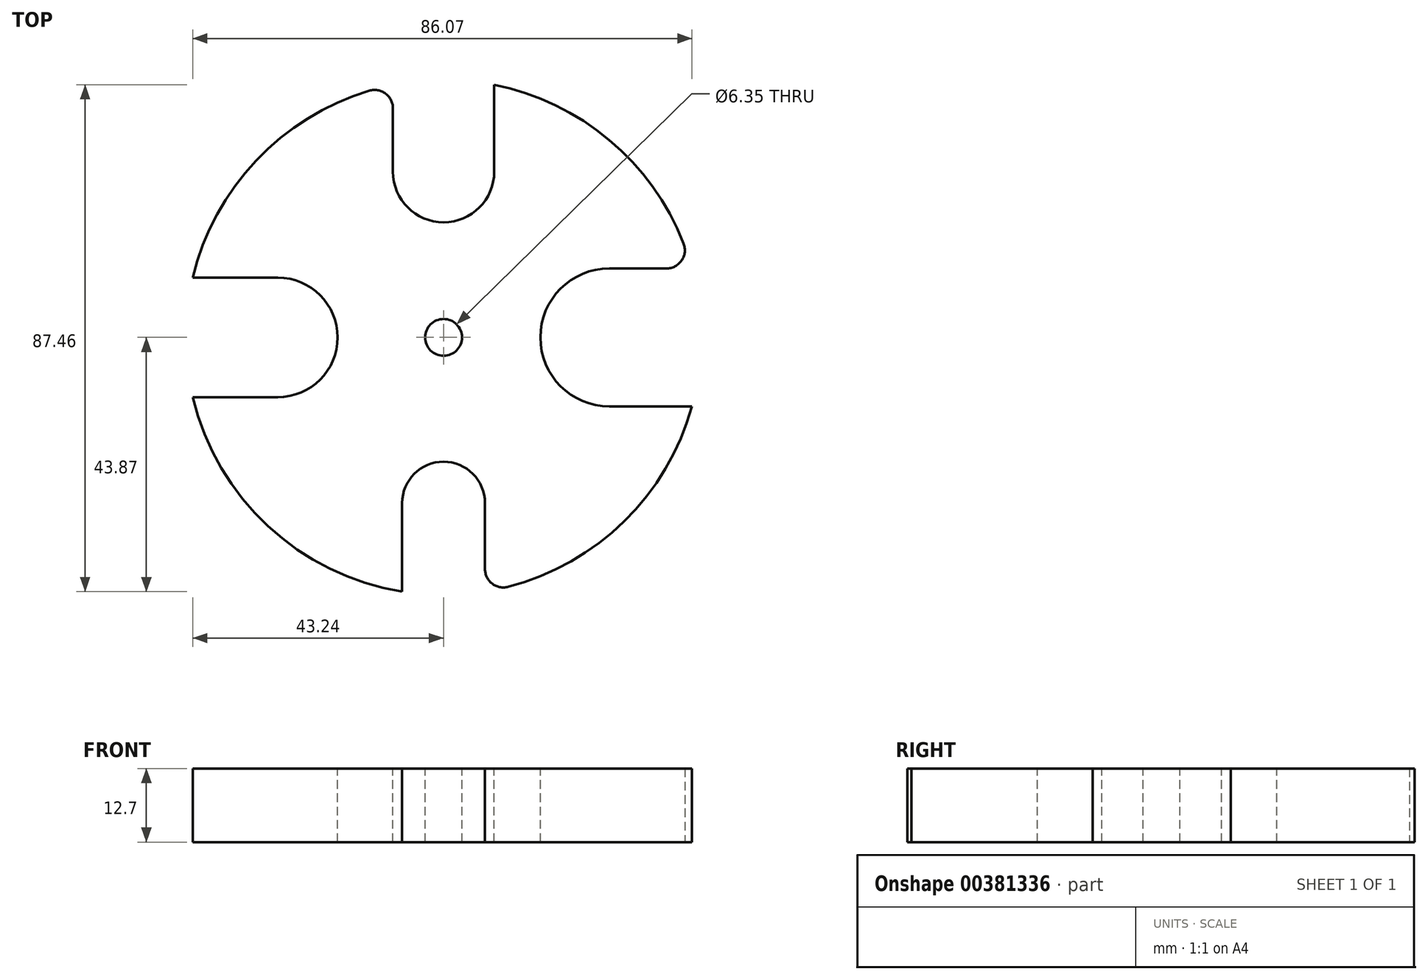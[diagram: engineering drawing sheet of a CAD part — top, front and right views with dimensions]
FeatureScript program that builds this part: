
annotation { "Feature Type Name" : "Feature", "Feature Type Description" : "" }
export const myFeature = defineFeature(function(context is Context, id is Id, definition is map)
    precondition{}
    {
        {
            var Q0;
            Q0=qCreatedBy(makeId("Top.planeOp"),FACE);
            var sketch = newSketch(context, id + "F0", { "sketchPlane" : qUnion([Q0])});
            skCircle(sketch, "E0", {"center": v(0, 0) * mm, "radius": 44.45 * mm});
            skSolve(sketch);
        }
        {
            var Q0;
            Q0=makeQuery(id+"F0.imprint","IMPRINT",FACE,{"disambiguationData":[TD([[makeQuery(id+"F0.imprint","IMPRINT",EDGE,{"derivedFrom":sQuery(id+"F0.wireOp",EDGE,"E0")}),1.0]])]});
            extrude(context, id + "F1", {"entities" : qUnion([Q0]), "depth" : 12.7 * mm});
        }
        {
            var Q0;
            Q0=makeQuery(id+"F1.opExtrude","CAP_FACE",FACE,{"disambiguationData":[OSD([sQuery(id+"F0.wireOp",EDGE,"E0")])],"isStart":false});
            var sketch = newSketch(context, id + "F2", { "sketchPlane" : qUnion([Q0])});
            skLineSegment(sketch, "E1", {"start": v(-28.58, 10.31) * mm, "end": v(-53.98, 10.31) * mm});
            skLineSegment(sketch, "E2", {"start": v(-53.98, 10.31) * mm, "end": v(-53.98, -10.31) * mm});
            skLineSegment(sketch, "E3", {"start": v(-53.98, -10.31) * mm, "end": v(-28.58, -10.31) * mm});
            skArc(sketch, "E4", {"start": v(-28.58, 10.31) * mm, "mid": v(-38.89, 0) * mm, "end": v(-28.57, -10.31) * mm, "construction": true});
            skArc(sketch, "E5", {"start": v(-28.58, -10.31) * mm, "mid": v(-18.26, 0) * mm, "end": v(-28.58, 10.31) * mm});
            skSolve(sketch);
        }
        {
            var Q0;
            {var subQ5=sQuery(id+"F2.wireOp",EDGE,"E5");Q0=makeQuery(id+"F2.imprint","IMPRINT",FACE,{"disambiguationData":[TD([[makeQuery(id+"F2.imprint","IMPRINT",EDGE,{"derivedFrom":subQ5}),1.0]])]});}
            extrude(context, id + "F3", {"entities" : qUnion([Q0]), "operationType" : NewBodyOperationType.REMOVE, "oppositeDirection" : true, "depth" : 12.7 * mm});
        }
        {
            var Q0;
            Q0=makeQuery(id+"F1.opExtrude","CAP_FACE",FACE,{"disambiguationData":[OSD([sQuery(id+"F0.wireOp",EDGE,"E0")])],"isStart":false});
            var sketch = newSketch(context, id + "F4", { "sketchPlane" : qUnion([Q0])});
            skLineSegment(sketch, "E6", {"start": v(28.59, 11.9) * mm, "end": v(53.99, 11.9) * mm});
            skLineSegment(sketch, "E7", {"start": v(53.99, 11.9) * mm, "end": v(53.99, -11.9) * mm});
            skLineSegment(sketch, "E8", {"start": v(53.99, -11.9) * mm, "end": v(28.59, -11.9) * mm});
            skArc(sketch, "E9", {"start": v(28.59, 11.9) * mm, "mid": v(16.69, 0) * mm, "end": v(28.59, -11.9) * mm});
            skArc(sketch, "E10", {"start": v(28.59, -11.9) * mm, "mid": v(40.49, 0) * mm, "end": v(28.59, 11.9) * mm, "construction": true});
            skSolve(sketch);
        }
        {
            var Q0;
            {var subQ5=sQuery(id+"F4.wireOp",EDGE,"E9");Q0=makeQuery(id+"F4.imprint","IMPRINT",FACE,{"disambiguationData":[TD([[makeQuery(id+"F4.imprint","IMPRINT",EDGE,{"derivedFrom":subQ5}),1.0]])]});}
            extrude(context, id + "F5", {"entities" : qUnion([Q0]), "operationType" : NewBodyOperationType.REMOVE, "oppositeDirection" : true, "depth" : 12.7 * mm});
        }
        {
            var Q0;
            Q0=makeQuery(id+"F1.opExtrude","CAP_FACE",FACE,{"disambiguationData":[OSD([sQuery(id+"F0.wireOp",EDGE,"E0")])],"isStart":false});
            var sketch = newSketch(context, id + "F6", { "sketchPlane" : qUnion([Q0])});
            skLineSegment(sketch, "E11", {"start": v(-8.72, 28.59) * mm, "end": v(-8.72, 53.99) * mm});
            skLineSegment(sketch, "E12", {"start": v(-8.72, 53.99) * mm, "end": v(8.72, 53.99) * mm});
            skLineSegment(sketch, "E13", {"start": v(8.72, 53.99) * mm, "end": v(8.72, 28.59) * mm});
            skArc(sketch, "E14", {"start": v(-8.72, 28.59) * mm, "mid": v(0, 19.86) * mm, "end": v(8.72, 28.59) * mm});
            skArc(sketch, "E15", {"start": v(8.72, 28.59) * mm, "mid": v(0, 37.31) * mm, "end": v(-8.72, 28.59) * mm, "construction": true});
            skSolve(sketch);
        }
        {
            var Q0;
            {var subQ6=sQuery(id+"F6.wireOp",EDGE,"E14");Q0=makeQuery(id+"F6.imprint","IMPRINT",FACE,{"disambiguationData":[TD([[makeQuery(id+"F6.imprint","IMPRINT",EDGE,{"derivedFrom":subQ6}),1.0]])]});}
            extrude(context, id + "F7", {"entities" : qUnion([Q0]), "operationType" : NewBodyOperationType.REMOVE, "oppositeDirection" : true, "depth" : 25.4 * mm});
        }
        {
            var Q0;
            Q0=makeQuery(id+"F1.opExtrude","CAP_FACE",FACE,{"disambiguationData":[OSD([sQuery(id+"F0.wireOp",EDGE,"E0")])],"isStart":false});
            var sketch = newSketch(context, id + "F8", { "sketchPlane" : qUnion([Q0])});
            skLineSegment(sketch, "E16", {"start": v(-7.14, -28.58) * mm, "end": v(-7.14, -53.98) * mm});
            skLineSegment(sketch, "E17", {"start": v(-7.14, -53.98) * mm, "end": v(7.14, -53.98) * mm});
            skLineSegment(sketch, "E18", {"start": v(7.14, -53.98) * mm, "end": v(7.14, -28.58) * mm});
            skArc(sketch, "E19", {"start": v(-7.14, -28.58) * mm, "mid": v(0, -35.71) * mm, "end": v(7.14, -28.58) * mm, "construction": true});
            skArc(sketch, "E20", {"start": v(7.14, -28.58) * mm, "mid": v(0, -21.44) * mm, "end": v(-7.14, -28.58) * mm});
            skSolve(sketch);
        }
        {
            var Q0;
            {var subQ6=sQuery(id+"F8.wireOp",EDGE,"E20");Q0=makeQuery(id+"F8.imprint","IMPRINT",FACE,{"disambiguationData":[TD([[makeQuery(id+"F8.imprint","IMPRINT",EDGE,{"derivedFrom":subQ6}),1.0]])]});}
            extrude(context, id + "F9", {"entities" : qUnion([Q0]), "operationType" : NewBodyOperationType.REMOVE, "oppositeDirection" : true, "depth" : 12.7 * mm});
        }
        {
            var Q0;
            Q0=makeQuery(id+"F1.opExtrude","CAP_FACE",FACE,{"disambiguationData":[OSD([sQuery(id+"F0.wireOp",EDGE,"E0")])],"isStart":false});
            var sketch = newSketch(context, id + "F10", { "sketchPlane" : qUnion([Q0])});
            skCircle(sketch, "E21", {"center": v(0, 0) * mm, "radius": 3.17 * mm});
            skSolve(sketch);
        }
        {
            var Q0;
            Q0=qSketchRegion(id+"F10",true);
            extrude(context, id + "F11", {"entities" : qUnion([Q0]), "operationType" : NewBodyOperationType.REMOVE, "endBound" : BoundingType.UP_TO_NEXT, "oppositeDirection" : true, "depth" : 12.7 * mm});
        }
        {
            var Q0;
            Q0=makeQuery(id+"F5.boolean.opBoolean","COPY",EDGE,{"derivedFrom":makeQuery(id+"F5.opExtrude","SWEPT_EDGE",EDGE,{"disambiguationData":[OSD([sQuery(id+"F0.wireOp",EDGE,"E0"),sQuery(id+"F4.wireOp",EDGE,"E8")])]})});
            var Q1;
            Q1=makeQuery(id+"F5.boolean.opBoolean","COPY",EDGE,{"derivedFrom":makeQuery(id+"F5.opExtrude","SWEPT_EDGE",EDGE,{"disambiguationData":[OSD([sQuery(id+"F0.wireOp",EDGE,"E0"),sQuery(id+"F4.wireOp",EDGE,"E6")])]})});
            var Q2;
            Q2=makeQuery(id+"F7.boolean.opBoolean","COPY",EDGE,{"derivedFrom":makeQuery(id+"F7.opExtrude","SWEPT_EDGE",EDGE,{"disambiguationData":[OSD([sQuery(id+"F0.wireOp",EDGE,"E0"),sQuery(id+"F6.wireOp",EDGE,"E13")])]})});
            var Q3;
            Q3=makeQuery(id+"F7.boolean.opBoolean","COPY",EDGE,{"derivedFrom":makeQuery(id+"F7.opExtrude","SWEPT_EDGE",EDGE,{"disambiguationData":[OSD([sQuery(id+"F0.wireOp",EDGE,"E0"),sQuery(id+"F6.wireOp",EDGE,"E11")])]})});
            var Q4;
            Q4=makeQuery(id+"F9.boolean.opBoolean","COPY",EDGE,{"derivedFrom":makeQuery(id+"F9.opExtrude","SWEPT_EDGE",EDGE,{"disambiguationData":[OSD([sQuery(id+"F0.wireOp",EDGE,"E0"),sQuery(id+"F8.wireOp",EDGE,"E18")])]})});
            var Q5;
            Q5=makeQuery(id+"F9.boolean.opBoolean","COPY",EDGE,{"derivedFrom":makeQuery(id+"F9.opExtrude","SWEPT_EDGE",EDGE,{"disambiguationData":[OSD([sQuery(id+"F0.wireOp",EDGE,"E0"),sQuery(id+"F8.wireOp",EDGE,"E16")])]})});
            var Q6;
            Q6=makeQuery(id+"F3.boolean.opBoolean","COPY",EDGE,{"derivedFrom":makeQuery(id+"F3.opExtrude","SWEPT_EDGE",EDGE,{"disambiguationData":[OSD([sQuery(id+"F0.wireOp",EDGE,"E0"),sQuery(id+"F2.wireOp",EDGE,"E3")])]})});
            var Q7;
            Q7=makeQuery(id+"F3.boolean.opBoolean","COPY",EDGE,{"derivedFrom":makeQuery(id+"F3.opExtrude","SWEPT_EDGE",EDGE,{"disambiguationData":[OSD([sQuery(id+"F0.wireOp",EDGE,"E0"),sQuery(id+"F2.wireOp",EDGE,"E1")])]})});
            fillet(context, id + "F12", {"entities" : qUnion([Q0, Q1, Q2, Q3, Q4, Q5, Q6, Q7]), "radius" : 3.17 * mm, "tangentPropagation" : true, "allowEdgeOverflow" : false});
        }
    });
